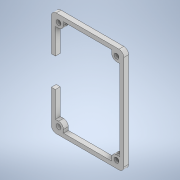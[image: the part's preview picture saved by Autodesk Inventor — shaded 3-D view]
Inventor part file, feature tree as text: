
AUTODESK INVENTOR PART (.ipt)
format: ipt  version: 2021.2 (Build 252289000, 289)  size: 149,504 bytes
history: native  units: mm
features: reference x9, other x3, extrude x1, sketch x1
ambient origin geometry x8: Origin, YZ Plane, XZ Plane, XY Plane, X Axis, Y Axis, Z Axis, Center Point
bodies: Body1 (feature_tree)
feature tree (14):
  other  "Твердое тело1"
  extrude  "Выдавливание1"  Depth=45.0mm
  sketch  "Эскиз1"
  reference  "Ссылка1"
  reference  "Ссылка2"
  reference  "Ссылка3"
  reference  "Ссылка4"
  reference  "Ссылка5"
  reference  "Ссылка6"
  reference  "Ссылка7"
  reference  "Ссылка8"
  reference  "Ссылка9"
  other  "Сборка1"
  other  "plate:1"
